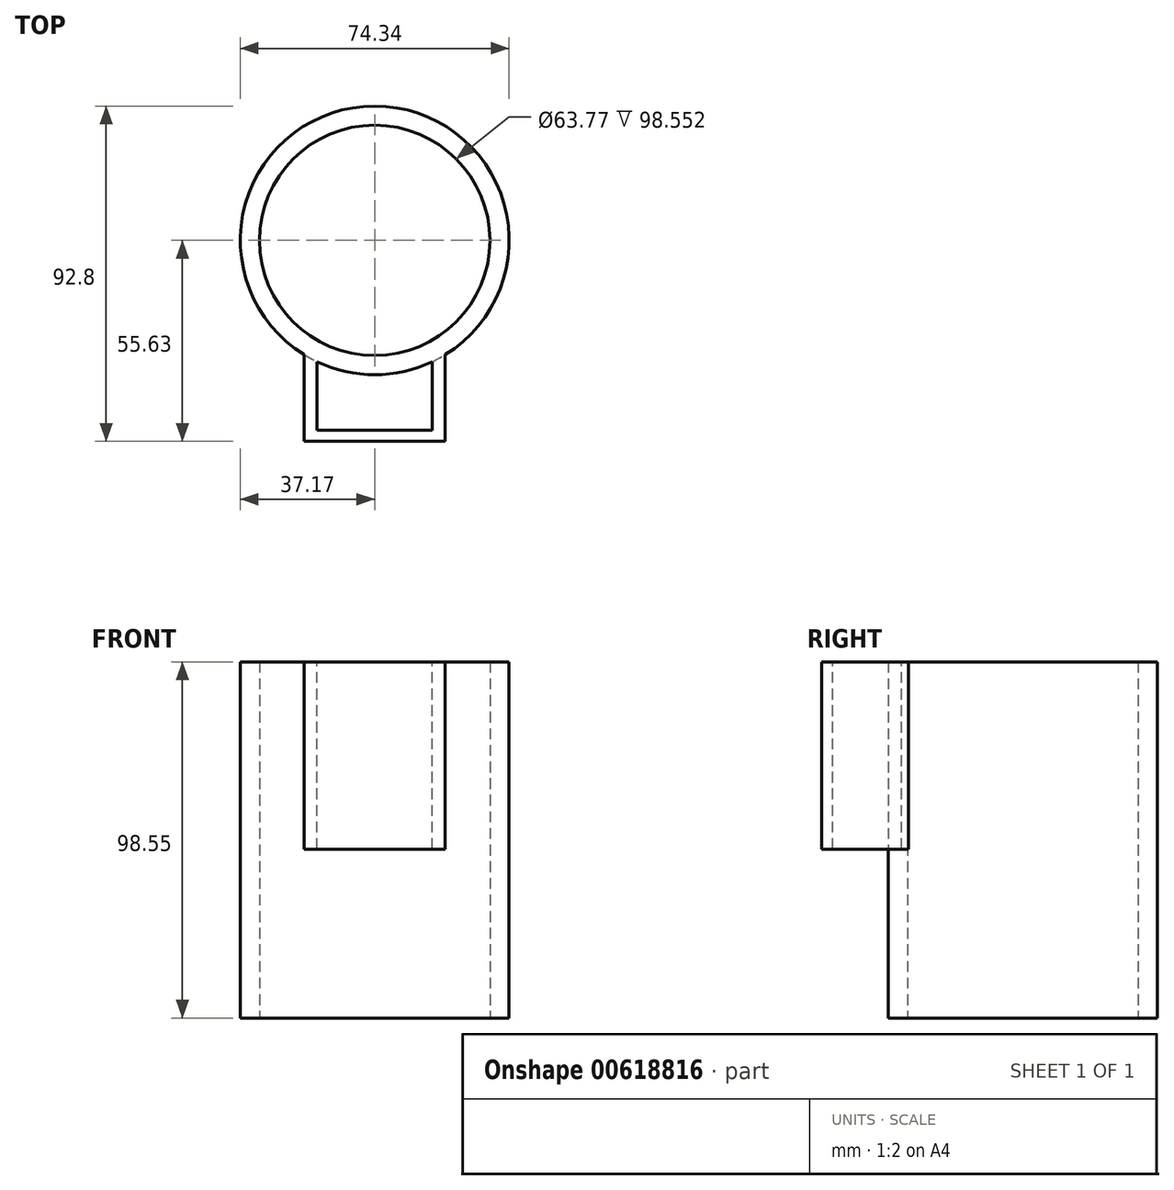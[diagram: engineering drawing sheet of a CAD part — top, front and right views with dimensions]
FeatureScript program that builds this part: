
annotation { "Feature Type Name" : "Feature", "Feature Type Description" : "" }
export const myFeature = defineFeature(function(context is Context, id is Id, definition is map)
    precondition{}
    {
        {
            var Q0;
            Q0=qCreatedBy(makeId("Top.planeOp"),FACE);
            var sketch = newSketch(context, id + "F0", { "sketchPlane" : qUnion([Q0])});
            skCircle(sketch, "E0", {"center": v(0, 0) * mm, "radius": 37.17 * mm});
            skCircle(sketch, "E1", {"center": v(0, 0) * mm, "radius": 31.88 * mm});
            skSolve(sketch);
        }
        {
            var Q0;
            Q0=qSketchRegion(id+"F0",true);
            extrude(context, id + "F1", {"entities" : qUnion([Q0]), "depth" : 98.55 * mm, "offsetDistance" : 25.4 * mm});
        }
        {
            var Q0;
            Q0=makeQuery(id+"F1.opExtrude","CAP_FACE",FACE,{"disambiguationData":[OSD([sQuery(id+"F0.wireOp",EDGE,"E0"),sQuery(id+"F0.wireOp",EDGE,"E1")])],"isStart":false});
            var sketch = newSketch(context, id + "F2", { "sketchPlane" : qUnion([Q0])});
            skLineSegment(sketch, "E2.bottom", {"start": v(19.52, -55.63) * mm, "end": v(-19.52, -55.63) * mm});
            skPoint(sketch, "E2.middle", {"position": v(0, -37.17) * mm});
            skLineSegment(sketch, "E3.bottom", {"start": v(15.95, -52.56) * mm, "end": v(-15.95, -52.56) * mm});
            skPoint(sketch, "E3.right.end.orphan", {"position": v(-15.95, -21.78) * mm});
            skPoint(sketch, "E2.right.end.orphan", {"position": v(-19.52, -18.7) * mm});
            skPoint(sketch, "E3.left.end.orphan", {"position": v(15.95, -21.78) * mm});
            skPoint(sketch, "E2.left.end.orphan", {"position": v(19.52, -18.7) * mm});
            skLineSegment(sketch, "E4", {"start": v(-15.95, -52.56) * mm, "end": v(-15.95, -33.57) * mm});
            skLineSegment(sketch, "E5", {"start": v(15.95, -52.56) * mm, "end": v(15.95, -33.57) * mm});
            skLineSegment(sketch, "E6", {"start": v(-19.52, -55.63) * mm, "end": v(-19.52, -31.63) * mm});
            skLineSegment(sketch, "E7", {"start": v(19.52, -55.63) * mm, "end": v(19.52, -31.63) * mm});
            skSolve(sketch);
        }
        {
            var Q0;
            Q0=makeQuery(id+"F2.imprint","IMPRINT",FACE,{"disambiguationData":[TD([[makeQuery(id+"F2.imprint","IMPRINT",EDGE,{"derivedFrom":sQuery(id+"F2.wireOp",EDGE,"E2.bottom")}),-1.0]])]});
            extrude(context, id + "F3", {"entities" : qUnion([Q0]), "operationType" : NewBodyOperationType.ADD, "oppositeDirection" : true, "depth" : 51.82 * mm, "offsetDistance" : 25.4 * mm});
        }
    });
